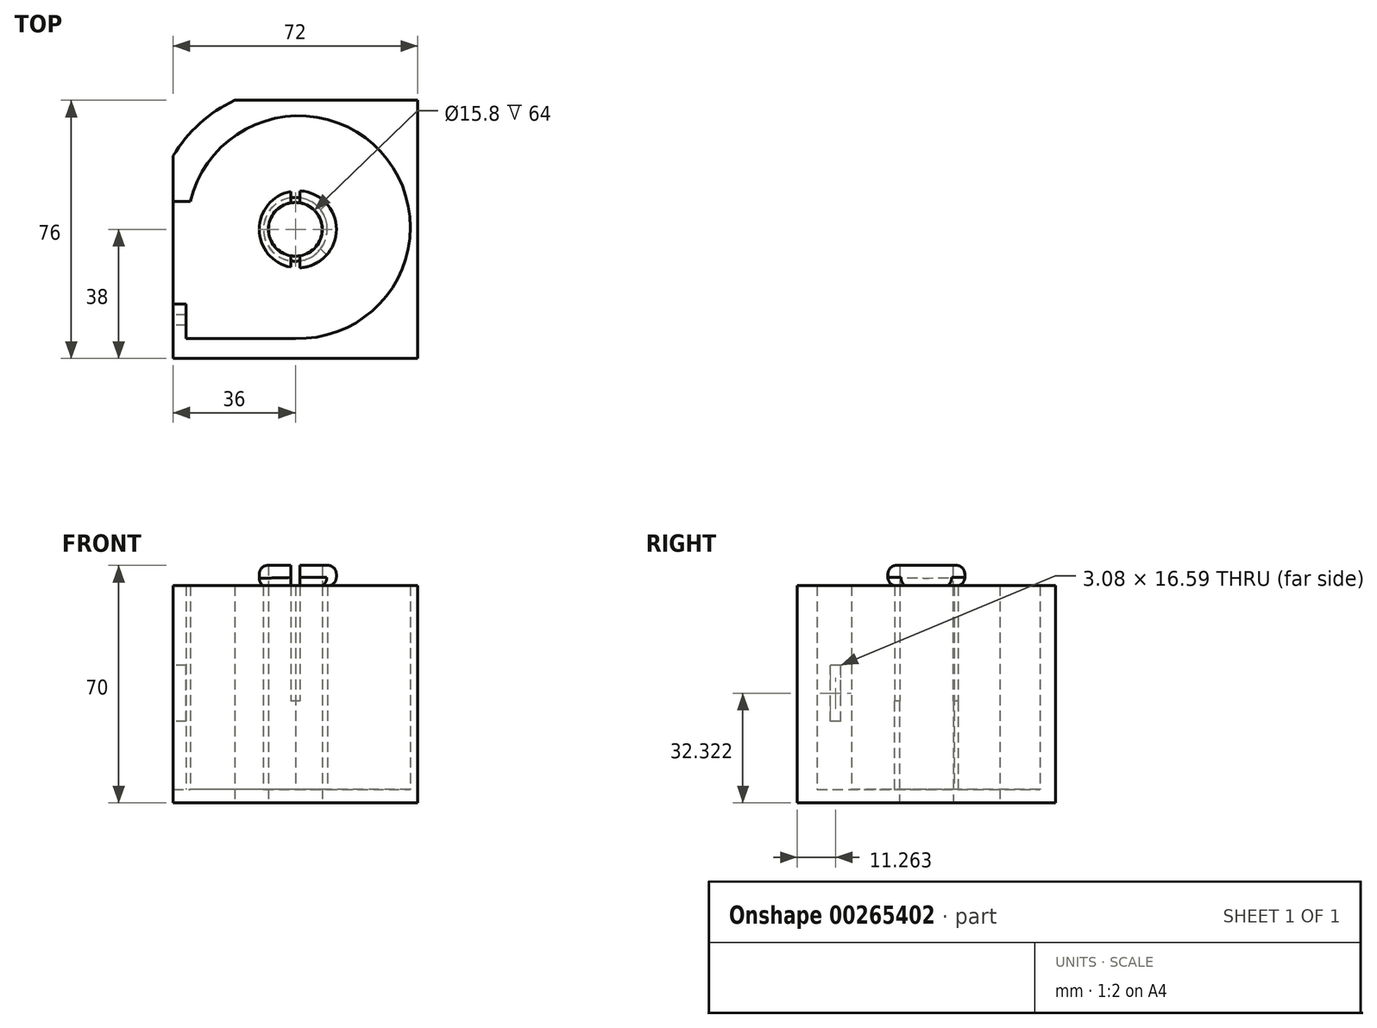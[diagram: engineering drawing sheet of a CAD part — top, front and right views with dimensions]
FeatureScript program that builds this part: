
annotation { "Feature Type Name" : "Feature", "Feature Type Description" : "" }
export const myFeature = defineFeature(function(context is Context, id is Id, definition is map)
    precondition{}
    {
        {
            var Q0;
            Q0=qCreatedBy(makeId("Top.planeOp"),FACE);
            var sketch = newSketch(context, id + "F0", { "sketchPlane" : qUnion([Q0])});
            skLineSegment(sketch, "E0.bottom", {"start": v(-17.89, 38) * mm, "end": v(36, 38) * mm});
            skLineSegment(sketch, "E0.top", {"start": v(-36, -38) * mm, "end": v(36, -38) * mm});
            skLineSegment(sketch, "E0.left", {"start": v(-36, 21.63) * mm, "end": v(-36, -38) * mm});
            skLineSegment(sketch, "E0.right", {"start": v(36, 38) * mm, "end": v(36, -38) * mm});
            skPoint(sketch, "E0.middle", {"position": v(0, 0) * mm});
            skCircle(sketch, "E1", {"center": v(0, 0) * mm, "radius": 7.9 * mm});
            skArc(sketch, "E2", {"start": v(-17.89, 38) * mm, "mid": v(-28.16, 31.16) * mm, "end": v(-36, 21.63) * mm});
            skPoint(sketch, "E3.orphan", {"position": v(-36, 38) * mm});
            skSolve(sketch);
        }
        {
            var Q0;
            Q0 = qSketchRegion(id + "F0", true);
            extrude(context, id + "F1", {"entities" : qUnion([Q0]), "depth" : 4 * mm, "offsetDistance" : 25 * mm});
        }
        {
            var Q0;
            Q0=makeQuery(id+"F1.opExtrude","CAP_FACE",FACE,{"disambiguationData":[OSD([sQuery(id+"F0.wireOp",EDGE,"E0.bottom"),sQuery(id+"F0.wireOp",EDGE,"E0.top"),sQuery(id+"F0.wireOp",EDGE,"E0.left"),sQuery(id+"F0.wireOp",EDGE,"E0.right"),sQuery(id+"F0.wireOp",EDGE,"E1"),sQuery(id+"F0.wireOp",EDGE,"E2")])],"isStart":false});
            var sketch = newSketch(context, id + "F2", { "sketchPlane" : qUnion([Q0])});
            skCircle(sketch, "E4", {"center": v(0, 0) * mm, "radius": 7.9 * mm});
            skCircle(sketch, "E5", {"center": v(0, 0) * mm, "radius": 9.4 * mm});
            skArc(sketch, "E6", {"start": v(-17.89, 38) * mm, "mid": v(-28.16, 31.16) * mm, "end": v(-36, 21.63) * mm});
            skArc(sketch, "E7", {"start": v(0, -32.15) * mm, "mid": v(27.04, 20.6) * mm, "end": v(-30.92, 8.17) * mm});
            skLineSegment(sketch, "E8", {"start": v(-36, 21.63) * mm, "end": v(-36, 8.17) * mm});
            skLineSegment(sketch, "E9", {"start": v(-36, -38) * mm, "end": v(36, -38) * mm});
            skLineSegment(sketch, "E10", {"start": v(36, -38) * mm, "end": v(36, 38) * mm});
            skLineSegment(sketch, "E11", {"start": v(36, 38) * mm, "end": v(-17.89, 38) * mm});
            skLineSegment(sketch, "E12", {"start": v(-32.14, -32.15) * mm, "end": v(-32.14, -29.07) * mm});
            skLineSegment(sketch, "E13.trimOffspring", {"start": v(-36, -29.07) * mm, "end": v(-36, -38) * mm});
            skLineSegment(sketch, "E14", {"start": v(-36, 8.17) * mm, "end": v(-30.92, 8.17) * mm});
            skLineSegment(sketch, "E15", {"start": v(0, -32.15) * mm, "end": v(-32.14, -32.15) * mm});
            skLineSegment(sketch, "E16", {"start": v(-32.14, -29.07) * mm, "end": v(-32.14, -21.99) * mm});
            skLineSegment(sketch, "E17", {"start": v(-36, -29.07) * mm, "end": v(-36, -21.99) * mm});
            skLineSegment(sketch, "E18", {"start": v(-36, -21.99) * mm, "end": v(-32.14, -21.99) * mm});
            skPoint(sketch, "E19.orphan", {"position": v(-32.14, -21.9) * mm});
            skSolve(sketch);
        }
        {
            var Q0;
            Q0 = qSketchRegion(id + "F2", true);
            extrude(context, id + "F3", {"entities" : qUnion([Q0]), "operationType" : NewBodyOperationType.ADD, "depth" : 60 * mm, "offsetDistance" : 25 * mm});
        }
        {
            var Q0;
            Q0=makeQuery(id+"F3.boolean.opBoolean","MERGE",FACE,{"derivedFrom":[makeQuery(id+"F1.opExtrude","SWEPT_FACE",FACE,{"disambiguationData":[OSD([sQuery(id+"F0.wireOp",EDGE,"E0.left")])]}),makeQuery(id+"F3.opExtrude","SWEPT_FACE",FACE,{"disambiguationData":[OSD([sQuery(id+"F2.wireOp",EDGE,"E8")])]}),makeQuery(id+"F3.opExtrude","SWEPT_FACE",FACE,{"disambiguationData":[OSD([sQuery(id+"F2.wireOp",EDGE,"E13.trimOffspring"),sQuery(id+"F2.wireOp",EDGE,"E17")])]})]});
            var sketch = newSketch(context, id + "F4", { "sketchPlane" : qUnion([Q0])});
            skLineSegment(sketch, "E20.bottom", {"start": v(25.2, 24.02) * mm, "end": v(28.28, 24.02) * mm});
            skLineSegment(sketch, "E20.top", {"start": v(25.2, 40.62) * mm, "end": v(28.28, 40.62) * mm});
            skLineSegment(sketch, "E20.left", {"start": v(25.2, 24.02) * mm, "end": v(25.2, 40.62) * mm});
            skLineSegment(sketch, "E20.right", {"start": v(28.28, 24.02) * mm, "end": v(28.28, 40.62) * mm});
            skSolve(sketch);
        }
        {
            var Q0;
            Q0 = qSketchRegion(id + "F4", true);
            extrude(context, id + "F5", {"entities" : qUnion([Q0]), "operationType" : NewBodyOperationType.REMOVE, "oppositeDirection" : true, "depth" : 25 * mm, "offsetDistance" : 25 * mm});
        }
        {
            var Q0;
            Q0=makeQuery(id+"F3.opExtrude","CAP_FACE",FACE,{"disambiguationData":[OSD([sQuery(id+"F2.wireOp",EDGE,"E4"),sQuery(id+"F2.wireOp",EDGE,"E5")])],"isStart":false});
            var sketch = newSketch(context, id + "F6", { "sketchPlane" : qUnion([Q0])});
            skCircle(sketch, "E21", {"center": v(0, 0) * mm, "radius": 7.96 * mm});
            skCircle(sketch, "E22", {"center": v(0.72, 0) * mm, "radius": 11.34 * mm});
            skSolve(sketch);
        }
        {
            var Q0;
            Q0 = qSketchRegion(id + "F6", true);
            extrude(context, id + "F7", {"entities" : qUnion([Q0]), "operationType" : NewBodyOperationType.ADD, "depth" : 6 * mm, "offsetDistance" : 25 * mm});
        }
        {
            var Q0;
            Q0=makeQuery(id+"F7.opExtrude","CAP_EDGE",EDGE,{"disambiguationData":[OSD([sQuery(id+"F6.wireOp",EDGE,"E22")])],"isStart":false});
            var Q1;
            Q1=makeQuery(id+"F7.opExtrude","CAP_EDGE",EDGE,{"disambiguationData":[OSD([sQuery(id+"F6.wireOp",EDGE,"E22")])],"isStart":true});
            fillet(context, id + "F8", {"entities" : qUnion([Q0, Q1]), "tangentPropagation" : true, "radius" : 2.5 * mm, "defaultsChanged" : true, "vertexSettings" : [], "allowEdgeOverflow" : false});
        }
        {
            var Q0;
            Q0=makeQuery(id+"F7.opExtrude","CAP_FACE",FACE,{"disambiguationData":[OSD([sQuery(id+"F6.wireOp",EDGE,"E21"),sQuery(id+"F6.wireOp",EDGE,"E22")])],"isStart":false});
            var sketch = newSketch(context, id + "F9", { "sketchPlane" : qUnion([Q0])});
            skLineSegment(sketch, "E23.bottom", {"start": v(1.39, 13.7) * mm, "end": v(-1.39, 13.7) * mm});
            skLineSegment(sketch, "E23.top", {"start": v(1.39, -13.7) * mm, "end": v(-1.39, -13.7) * mm});
            skLineSegment(sketch, "E23.left", {"start": v(1.39, 13.7) * mm, "end": v(1.39, -13.7) * mm});
            skLineSegment(sketch, "E23.right", {"start": v(-1.39, 13.7) * mm, "end": v(-1.39, -13.7) * mm});
            skPoint(sketch, "E23.middle", {"position": v(0, 0) * mm});
            skSolve(sketch);
        }
        {
            var Q0;
            Q0 = qSketchRegion(id + "F9", true);
            extrude(context, id + "F10", {"entities" : qUnion([Q0]), "operationType" : NewBodyOperationType.REMOVE, "oppositeDirection" : true, "depth" : 40 * mm, "offsetDistance" : 25 * mm});
        }
    });
